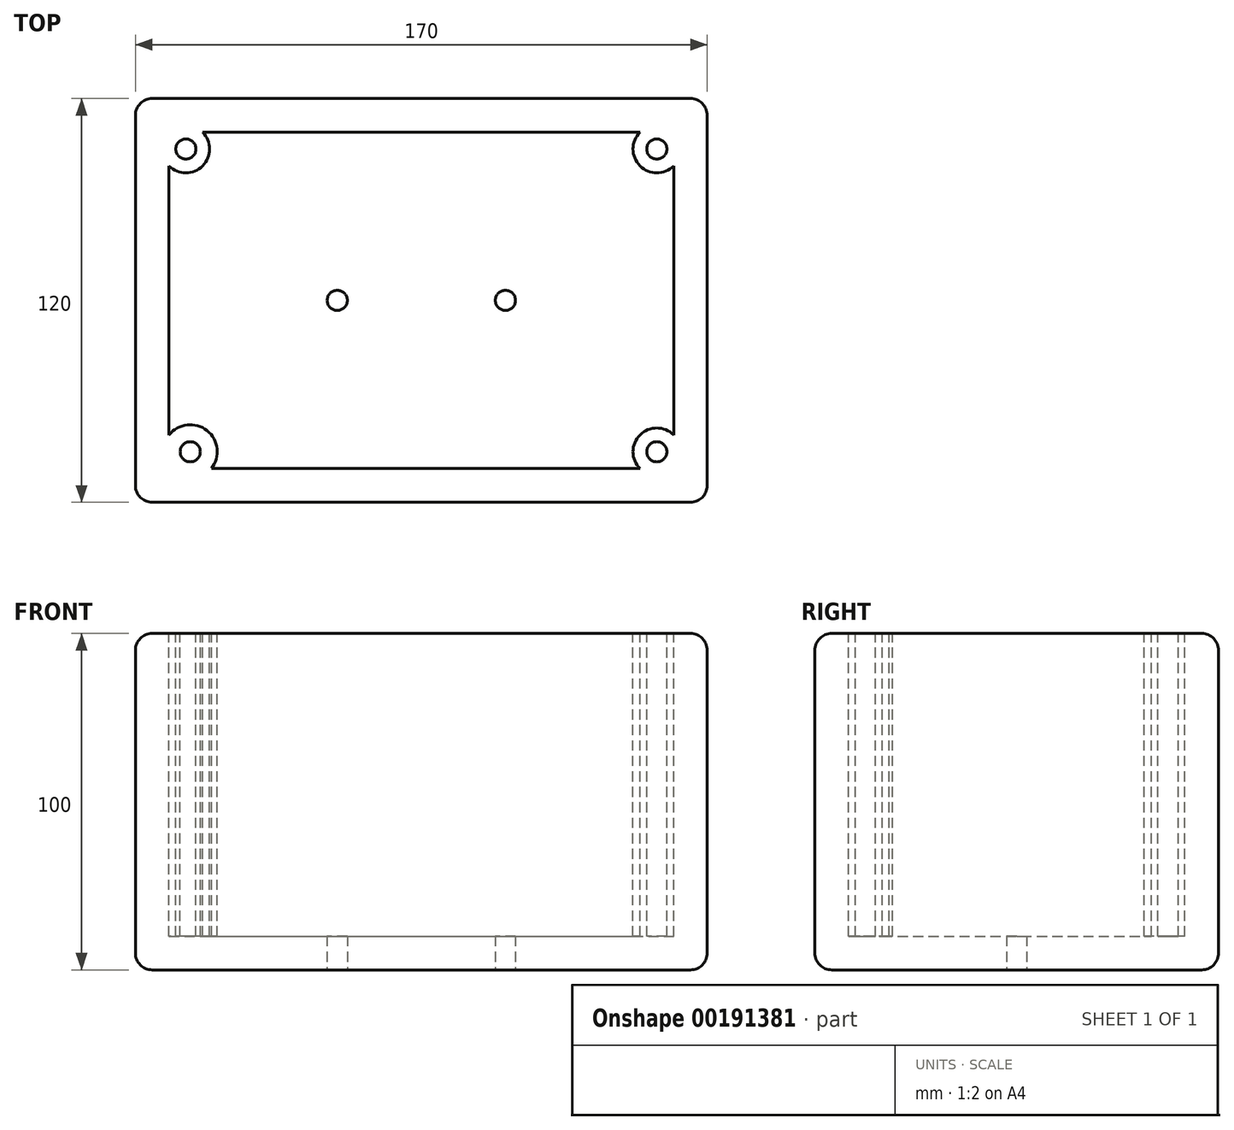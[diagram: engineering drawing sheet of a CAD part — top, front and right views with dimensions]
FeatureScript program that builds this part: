
annotation { "Feature Type Name" : "Feature", "Feature Type Description" : "" }
export const myFeature = defineFeature(function(context is Context, id is Id, definition is map)
    precondition{}
    {
        {
            var Q0;
            Q0=qCreatedBy(makeId("Front.planeOp"),FACE);
            var sketch = newSketch(context, id + "F0", { "sketchPlane" : qUnion([Q0])});
            skLineSegment(sketch, "E0.bottom", {"start": v(-85, 50) * mm, "end": v(85, 50) * mm});
            skLineSegment(sketch, "E0.top", {"start": v(-85, -50) * mm, "end": v(85, -50) * mm});
            skLineSegment(sketch, "E0.left", {"start": v(-85, 50) * mm, "end": v(-85, -50) * mm});
            skLineSegment(sketch, "E0.right", {"start": v(85, 50) * mm, "end": v(85, -50) * mm});
            skPoint(sketch, "E0.middle", {"position": v(0, 0) * mm});
            skSolve(sketch);
        }
        {
            var Q0;
            Q0=makeQuery(id+"F0.imprint","IMPRINT",FACE,{"disambiguationData":[TD([[makeQuery(id+"F0.imprint","IMPRINT",EDGE,{"derivedFrom":sQuery(id+"F0.wireOp",EDGE,"E0.bottom")}),-1.0]])]});
            extrude(context, id + "F1", {"entities" : qUnion([Q0]), "endBound" : BoundingType.SYMMETRIC, "depth" : 120 * mm});
        }
        {
            var Q0;
            Q0=makeQuery(id+"F1.opExtrude","SWEPT_FACE",FACE,{"disambiguationData":[OSD([sQuery(id+"F0.wireOp",EDGE,"E0.bottom")])]});
            shell(context, id + "F2", {"entities" : qUnion([Q0]), "thickness" : 10 * mm});
        }
        {
            var Q0;
            Q0=makeQuery(id+"F1.opExtrude","SWEPT_EDGE",EDGE,{"disambiguationData":[OSD([sQuery(id+"F0.wireOp",EDGE,"E0.bottom"),sQuery(id+"F0.wireOp",EDGE,"E0.left")])]});
            var Q1;
            Q1=makeQuery(id+"F1.opExtrude","CAP_EDGE",EDGE,{"disambiguationData":[OSD([sQuery(id+"F0.wireOp",EDGE,"E0.bottom")])],"isStart":false});
            var Q2;
            Q2=makeQuery(id+"F1.opExtrude","SWEPT_EDGE",EDGE,{"disambiguationData":[OSD([sQuery(id+"F0.wireOp",EDGE,"E0.bottom"),sQuery(id+"F0.wireOp",EDGE,"E0.right")])]});
            var Q3;
            Q3=makeQuery(id+"F1.opExtrude","CAP_EDGE",EDGE,{"disambiguationData":[OSD([sQuery(id+"F0.wireOp",EDGE,"E0.bottom")])],"isStart":true});
            var Q4;
            Q4=makeQuery(id+"F1.opExtrude","SWEPT_FACE",FACE,{"disambiguationData":[OSD([sQuery(id+"F0.wireOp",EDGE,"E0.right")])]});
            var Q5;
            Q5=makeQuery(id+"F1.opExtrude","CAP_FACE",FACE,{"disambiguationData":[OSD([sQuery(id+"F0.wireOp",EDGE,"E0.bottom"),sQuery(id+"F0.wireOp",EDGE,"E0.top"),sQuery(id+"F0.wireOp",EDGE,"E0.left"),sQuery(id+"F0.wireOp",EDGE,"E0.right")])],"isStart":false});
            var Q6;
            Q6=makeQuery(id+"F1.opExtrude","SWEPT_FACE",FACE,{"disambiguationData":[OSD([sQuery(id+"F0.wireOp",EDGE,"E0.left")])]});
            var Q7;
            Q7=makeQuery(id+"F1.opExtrude","SWEPT_FACE",FACE,{"disambiguationData":[OSD([sQuery(id+"F0.wireOp",EDGE,"E0.top")])]});
            fillet(context, id + "F3", {"entities" : qUnion([Q0, Q1, Q2, Q3, Q4, Q5, Q6, Q7]), "radius" : 5 * mm, "tangentPropagation" : true, "allowEdgeOverflow" : false});
        }
        {
            var Q0;
            Q0=makeQuery(id+"F1.opExtrude","SWEPT_FACE",FACE,{"disambiguationData":[OSD([sQuery(id+"F0.wireOp",EDGE,"E0.bottom")])]});
            var sketch = newSketch(context, id + "F4", { "sketchPlane" : qUnion([Q0])});
            skLineSegment(sketch, "E1.bottom", {"start": v(-75, 50) * mm, "end": v(-65, 50) * mm});
            skLineSegment(sketch, "E1.left", {"start": v(-75, 50) * mm, "end": v(-75, 40) * mm});
            skLineSegment(sketch, "E2.bottom", {"start": v(75, 50) * mm, "end": v(65, 50) * mm});
            skLineSegment(sketch, "E2.left", {"start": v(75, 50) * mm, "end": v(75, 40) * mm});
            skLineSegment(sketch, "E3.bottom", {"start": v(75, -50) * mm, "end": v(65, -50) * mm});
            skLineSegment(sketch, "E3.left", {"start": v(75, -50) * mm, "end": v(75, -40) * mm});
            skLineSegment(sketch, "E4.bottom", {"start": v(-75, -50) * mm, "end": v(-62.4, -50) * mm});
            skLineSegment(sketch, "E4.left", {"start": v(-75, -50) * mm, "end": v(-75, -40) * mm});
            skArc(sketch, "E5", {"start": v(-75, 40) * mm, "mid": v(-65, 40) * mm, "end": v(-65, 50) * mm});
            skArc(sketch, "E6", {"start": v(65, 50) * mm, "mid": v(65, 40) * mm, "end": v(75, 40) * mm});
            skArc(sketch, "E7", {"start": v(75, -40) * mm, "mid": v(65, -40) * mm, "end": v(65, -50) * mm});
            skArc(sketch, "E8", {"start": v(-62.4, -50) * mm, "mid": v(-63.7, -38.7) * mm, "end": v(-75, -40) * mm});
            skCircle(sketch, "E9", {"center": v(-70, 45) * mm, "radius": 3 * mm});
            skCircle(sketch, "E10", {"center": v(70, 45) * mm, "radius": 3 * mm});
            skCircle(sketch, "E11", {"center": v(70, -45) * mm, "radius": 3 * mm});
            skCircle(sketch, "E12", {"center": v(-68.7, -45) * mm, "radius": 3 * mm});
            skSolve(sketch);
        }
        {
            var Q0;
            Q0=makeQuery(id+"F4.imprint","IMPRINT",FACE,{"disambiguationData":[TD([[makeQuery(id+"F4.imprint","IMPRINT",EDGE,{"derivedFrom":sQuery(id+"F4.wireOp",EDGE,"E1.bottom")}),-1.0]])]});
            var Q1;
            Q1=makeQuery(id+"F4.imprint","IMPRINT",FACE,{"disambiguationData":[TD([[makeQuery(id+"F4.imprint","IMPRINT",EDGE,{"derivedFrom":sQuery(id+"F4.wireOp",EDGE,"E2.bottom")}),-1.0]])]});
            var Q2;
            Q2=makeQuery(id+"F4.imprint","IMPRINT",FACE,{"disambiguationData":[TD([[makeQuery(id+"F4.imprint","IMPRINT",EDGE,{"derivedFrom":sQuery(id+"F4.wireOp",EDGE,"E3.bottom")}),1.0]])]});
            var Q3;
            Q3=makeQuery(id+"F4.imprint","IMPRINT",FACE,{"disambiguationData":[TD([[makeQuery(id+"F4.imprint","IMPRINT",EDGE,{"derivedFrom":sQuery(id+"F4.wireOp",EDGE,"E4.bottom")}),1.0]])]});
            var Q4;
            {var subQ11=sQuery(id+"F4.wireOp",EDGE,"E1.bottom");Q4=makeQuery(id+"F4.imprint","IMPRINT",FACE,{"disambiguationData":[TD([[makeQuery(id+"F4.imprint","IMPRINT",EDGE,{"derivedFrom":subQ11}),1.0]])]});}
            extrude(context, id + "F5", {"entities" : qUnion([Q0, Q1, Q2, Q3, Q4]), "operationType" : NewBodyOperationType.ADD, "endBound" : BoundingType.UP_TO_NEXT, "oppositeDirection" : true, "depth" : 25 * mm});
        }
        {
            var Q0;
            Q0=makeQuery(id+"F1.opExtrude","SWEPT_FACE",FACE,{"disambiguationData":[OSD([sQuery(id+"F0.wireOp",EDGE,"E0.top")])]});
            var sketch = newSketch(context, id + "F6", { "sketchPlane" : qUnion([Q0])});
            skCircle(sketch, "E13", {"center": v(-25, 0) * mm, "radius": 3 * mm});
            skCircle(sketch, "E14", {"center": v(25, 0) * mm, "radius": 3 * mm});
            skSolve(sketch);
        }
        {
            var Q0;
            Q0=sQuery(id+"F6.wireOp",VERTEX,"E13.center");
            var Q1;
            Q1=sQuery(id+"F6.wireOp",VERTEX,"E14.center");
            var Q2;
            Q2=makeQuery(id+"F1.opExtrude","SWEPT_BODY",BODY,{"disambiguationData":[OSD([sQuery(id+"F0.wireOp",EDGE,"E0.bottom"),sQuery(id+"F0.wireOp",EDGE,"E0.top"),sQuery(id+"F0.wireOp",EDGE,"E0.left"),sQuery(id+"F0.wireOp",EDGE,"E0.right")])]});
            hole(context, id + "F7", {"style" : HoleStyle.SIMPLE, "endStyle" : HoleEndStyle.THROUGH, "holeDiameter" : 6 * mm, "startFromSketch" : true, "locations" : qUnion([Q0, Q1]), "scope" : qUnion([Q2]), "isTappedThrough" : true});
        }
    });
